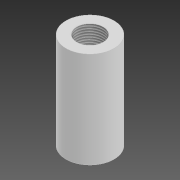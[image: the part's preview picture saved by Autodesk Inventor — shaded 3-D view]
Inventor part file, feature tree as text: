
AUTODESK INVENTOR PART (.ipt)
format: ipt  version: 2020 (Build 240168000, 168)  size: 105,984 bytes
history: native  units: in
note: dims shown in document units (in); Inventor stores cm internally (conversion verified against a paired STEP export)
features: extrude x2, thread x2, sketch x2, fillet x1
ambient origin geometry x8: Origin, YZ Plane, XZ Plane, XY Plane, X Axis, Y Axis, Z Axis, Center Point
bodies: Solid1 (feature_tree)
feature tree (7):
  extrude  "Extrusion1"  Depth=0.3937in
  extrude  "Extrusion2"  Depth=0.0394in
  thread  "Thread1"  [1 undecoded]
  fillet  "Fillet1"  Radius=0.5512in
  thread  "Thread3"  [1 undecoded]
  sketch  "Sketch1"  dims[d0=0.3937in d1=0.1181in]
  sketch  "Sketch2"  dims[d2=0.3937in d3=0.0in d4=0.2165in d5=0.3937in d6=0.0in d7=0.5512in d8=0.0in d11=0.0394in d12=0.5512in d13=0.0in]
note: 2 required parameter values undecoded (feature->parameter linkage not recoverable at this tier; creation-order binding heuristic only, values carry confidence <= 0.55)
